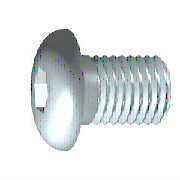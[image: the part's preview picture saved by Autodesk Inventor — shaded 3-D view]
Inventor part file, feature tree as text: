
AUTODESK INVENTOR PART (.ipt)
format: ipt  version: 2013 (Build 170138000, 138)  size: 188,416 bytes
history: native  units: mm (DEFAULTED — no unit token found)
features: sketch x2, extrude x1, plane x1
ambient origin geometry x7: Origin, YZ Plane, XY Plane, X Axis, Y Axis, Z Axis, Center Point
bodies: Solid1 (feature_tree), Body (feature_tree)
feature tree (4):
  extrude  "Slot"  Depth=0.49076mm
  plane  "Work Plane1"
  sketch  "Sketch1"  dims[d0=23.4mm d1=0.49076mm]
  sketch  "Sketch2"  dims[d2=2.75mm d3=1.56mm d4=60.0deg d5=5.0mm d6=5.0mm d7=3.464102mm d8=9.5mm d10=90.0deg d11=10.0mm d9=0.0mm d12=23.4mm d13=0.0mm d14=0.49076mm d15=0.49076mm d16=2.375mm d17=0.0mm d18=0.0mm d19=25.0mm d27=45.0deg d28=0.2mm d29=0.2mm]
